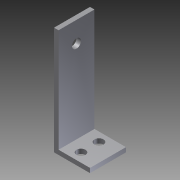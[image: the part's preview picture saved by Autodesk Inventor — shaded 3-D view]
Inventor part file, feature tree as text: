
AUTODESK INVENTOR PART (.ipt)
format: ipt  version: 2012 (Build 160160000, 160)  size: 96,768 bytes
history: native  units: in
note: dims shown in document units (in); Inventor stores cm internally (conversion verified against a paired STEP export)
features: extrude x3, sketch x3
ambient origin geometry x8: Origin, YZ Plane, XZ Plane, XY Plane, X Axis, Y Axis, Z Axis, Center Point
bodies: Solid1 (feature_tree)
feature tree (6):
  extrude  "Extrusion1"  Depth=0.125in
  extrude  "Extrusion2"  Depth=1.0in
  extrude  "Extrusion3"  Depth=0.5in
  sketch  "Sketch1"  dims[d0=0.125in d1=0.125in]
  sketch  "Sketch2"  dims[d2=3.0in d3=1.0in]
  sketch  "Sketch3"  dims[d4=1.0in d5=0.0in d6=0.5in d7=0.25in d8=0.25in d9=0.25in d10=0.25in d11=0.5in d12=1.0in d13=0.0in d14=0.25in d15=2.432in d16=0.5in d17=1.0in d18=0.0in]
